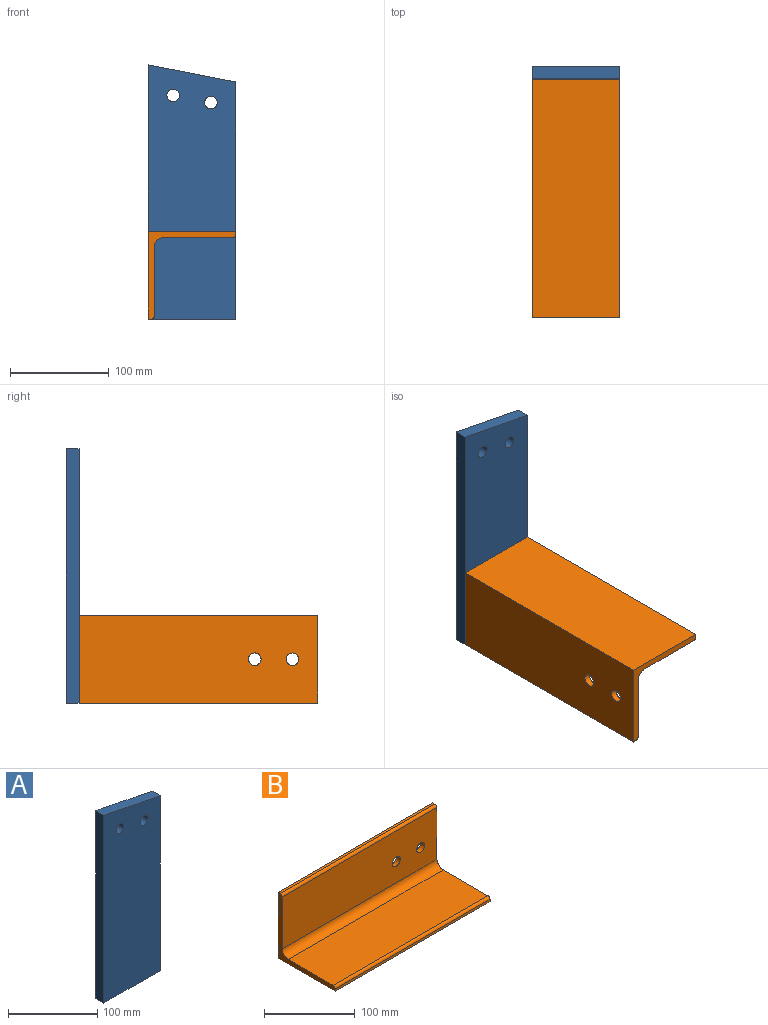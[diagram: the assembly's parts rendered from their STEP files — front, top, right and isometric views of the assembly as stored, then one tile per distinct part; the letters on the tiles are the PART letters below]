
ASSEMBLY  parts=2 mates=1
PART A: 8 faces, bbox 88.9x12.7x257.2 mm
  f0: plane 257.18x12.7mm, normal (-1,0,0), area 3266.1mm2, adj f1,f5,f6,f7
  f1: plane 88.9x12.7mm, normal (0,0,-1), area 1129mm2, adj f0,f2,f6,f7
  f2: plane 239.89x12.7mm, normal (1,0,0), area 3046.7mm2, adj f1,f5,f6,f7
  f3: cylinder r=6.35mm len=12.7mm, axis (0,1,0), area 506.7mm2, adj f6,f7
  f4: cylinder r=6.35mm len=12.7mm, axis (0,1,0), area 506.7mm2, adj f6,f7
  f5: plane 88.9x17.28mm, normal (0.19,0,0.98), area 1150.2mm2, adj f0,f2,f6,f7
  f6: plane 257.18x88.9mm, normal (0,-1,0), area 21841.4mm2, adj f0,f1,f2,f3,f4,f5
  f7: plane 257.18x88.9mm, normal (0,1,0), area 21841.4mm2, adj f0,f1,f2,f3,f4,f5
PART B: 13 faces, bbox 241.3x88.9x88.9 mm
  f0: plane 88.9x88.9mm, normal (1,0,0), area 1103.8mm2, adj f2,f3,f4,f5,f6,f7,f8,f9
  f1: plane 88.9x88.9mm, normal (-1,0,0), area 1103.8mm2, adj f2,f3,f4,f5,f6,f7,f8,f9
  f2: cylinder r=3.17mm len=241.3mm, axis (-1,0,0), area 1203.4mm2, adj f0,f1,f3,f10
  f3: plane 241.3x69.85mm, normal (0,0,1), area 16854.8mm2, adj f0,f1,f2,f4
  f4: cylinder r=9.52mm len=241.3mm, axis (-1,0,0), area 3610.3mm2, adj f0,f1,f3,f5
  f5: plane 241.3x69.85mm, normal (0,-1,0), area 16601.5mm2, adj f0,f1,f4,f6,f11,f12
  f6: cylinder r=3.17mm len=241.3mm, axis (-1,0,0), area 1203.4mm2, adj f0,f1,f5,f7
  f7: plane 241.3x3.18mm, normal (0,0,1), area 766.1mm2, adj f0,f1,f6,f8
  f8: plane 241.3x88.9mm, normal (0,1,0), area 21198.2mm2, adj f0,f1,f7,f9,f11,f12
  f9: plane 241.3x88.9mm, normal (0,0,-1), area 21451.6mm2, adj f0,f1,f8,f10
  f10: plane 241.3x3.18mm, normal (0,-1,0), area 766.1mm2, adj f0,f1,f2,f9
  f11: cylinder r=6.35mm len=12.7mm, axis (0,1,0), area 253.4mm2, adj f5,f8
  f12: cylinder r=6.35mm len=12.7mm, axis (0,1,0), area 253.4mm2, adj f5,f8
PLACE A at identity
PLACE B rot(axis=(0.71,-0.71,0),180deg) t=(-44.45,-254,-39.69)mm
MATE fastened B.f1 <-> A.f6  axis (0,1,0) through (0,-12.7,-39.69)mm
